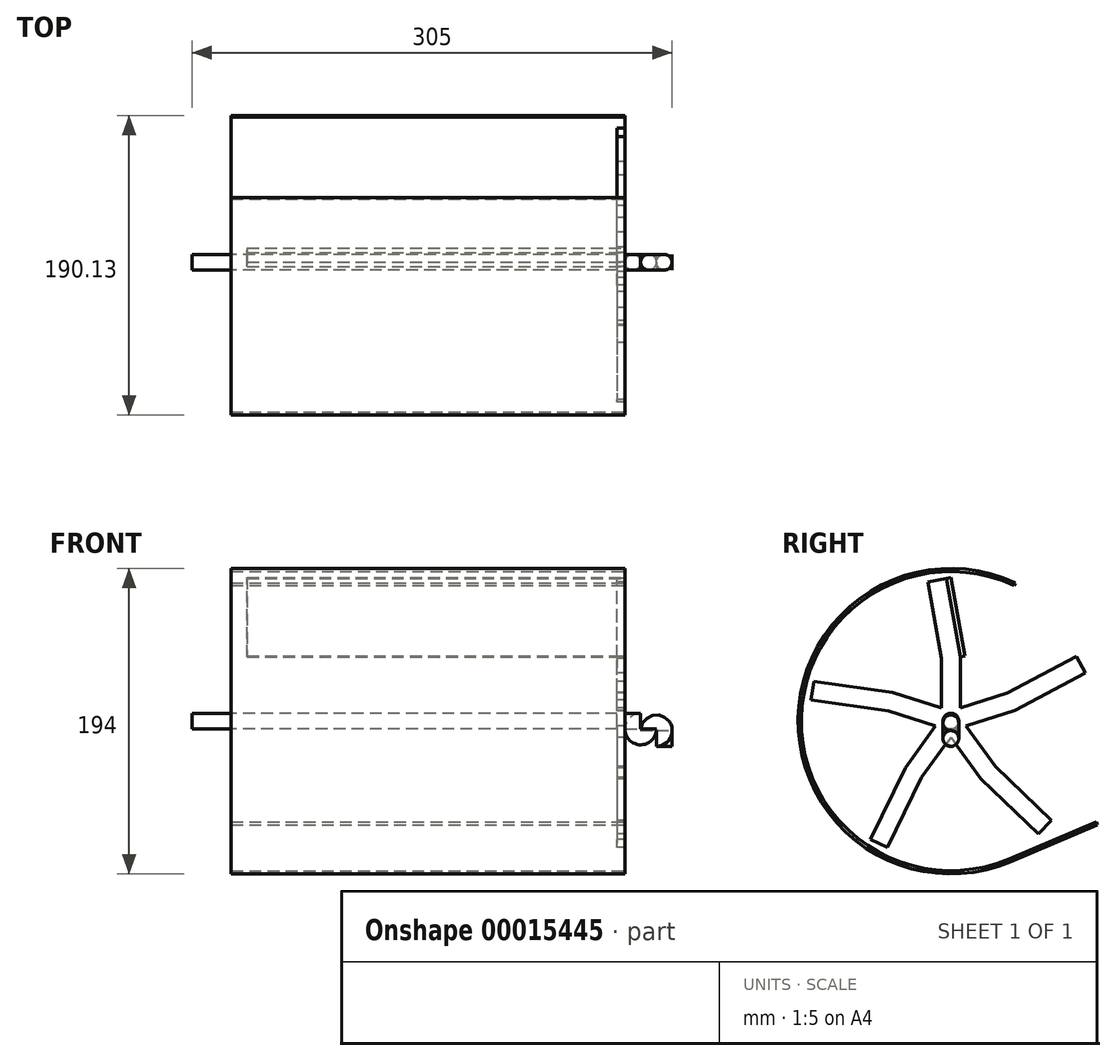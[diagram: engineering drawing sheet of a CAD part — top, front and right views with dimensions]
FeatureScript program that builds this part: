
annotation { "Feature Type Name" : "Feature", "Feature Type Description" : "" }
export const myFeature = defineFeature(function(context is Context, id is Id, definition is map)
    precondition{}
    {
        {
            var Q0;
            Q0=qCreatedBy(makeId("Right.planeOp"),FACE);
            var sketch = newSketch(context, id + "F0", { "sketchPlane" : qUnion([Q0])});
            skCircle(sketch, "E0", {"center": v(0, 0) * mm, "radius": 5 * mm});
            skSolve(sketch);
        }
        {
            var Q0;
            Q0 = qSketchRegion(id + "F0", true);
            extrude(context, id + "F1", {"entities" : qUnion([Q0]), "depth" : 270 * mm});
        }
        {
            var Q0;
            Q0=makeQuery(id+"F1.opExtrude","CAP_FACE",FACE,{"disambiguationData":[OSD([sQuery(id+"F0.wireOp",EDGE,"E0")])],"isStart":false});
            var sketch = newSketch(context, id + "F2", { "sketchPlane" : qUnion([Q0])});
            skLineSegment(sketch, "E1", {"start": v(0, 0) * mm, "end": v(0, 40.34) * mm, "construction": true});
            skLineSegment(sketch, "E2", {"start": v(0, 40.34) * mm, "end": v(-8.68, 89.58) * mm, "construction": true});
            skLineSegment(sketch, "E3.0", {"start": v(6, 40.86) * mm, "end": v(-2.77, 90.62) * mm});
            skLineSegment(sketch, "E3.1", {"start": v(6, 0) * mm, "end": v(6, 40.86) * mm});
            skLineSegment(sketch, "E4.0", {"start": v(-6, 39.81) * mm, "end": v(-14.6, 88.54) * mm});
            skLineSegment(sketch, "E4.1", {"start": v(-6, 0) * mm, "end": v(-6, 39.81) * mm});
            skLineSegment(sketch, "E5", {"start": v(-14.6, 88.54) * mm, "end": v(-2.77, 90.62) * mm});
            skLineSegment(sketch, "E6.1.0", {"start": v(1.85, 5.7) * mm, "end": v(-37.01, 18.33) * mm});
            skLineSegment(sketch, "E6.1.1", {"start": v(-37.01, 18.33) * mm, "end": v(-87.04, 25.37) * mm});
            skLineSegment(sketch, "E6.1.2", {"start": v(-88.71, 13.48) * mm, "end": v(-87.04, 25.37) * mm});
            skLineSegment(sketch, "E6.1.3", {"start": v(-39.72, 6.6) * mm, "end": v(-88.71, 13.48) * mm});
            skLineSegment(sketch, "E6.1.4", {"start": v(-1.85, -5.7) * mm, "end": v(-39.72, 6.6) * mm});
            skLineSegment(sketch, "E6.2.0", {"start": v(-4.85, 3.53) * mm, "end": v(-28.87, -29.53) * mm});
            skLineSegment(sketch, "E6.2.1", {"start": v(-28.87, -29.53) * mm, "end": v(-51.02, -74.95) * mm});
            skLineSegment(sketch, "E6.2.2", {"start": v(-40.24, -80.2) * mm, "end": v(-51.02, -74.95) * mm});
            skLineSegment(sketch, "E6.2.3", {"start": v(-18.55, -35.74) * mm, "end": v(-40.24, -80.2) * mm});
            skLineSegment(sketch, "E6.2.4", {"start": v(4.85, -3.53) * mm, "end": v(-18.55, -35.74) * mm});
            skLineSegment(sketch, "E6.3.0", {"start": v(-4.85, -3.53) * mm, "end": v(19.17, -36.59) * mm});
            skLineSegment(sketch, "E6.3.1", {"start": v(19.17, -36.59) * mm, "end": v(55.51, -71.68) * mm});
            skLineSegment(sketch, "E6.3.2", {"start": v(63.85, -63.05) * mm, "end": v(55.51, -71.68) * mm});
            skLineSegment(sketch, "E6.3.3", {"start": v(28.26, -28.68) * mm, "end": v(63.85, -63.05) * mm});
            skLineSegment(sketch, "E6.3.4", {"start": v(4.85, 3.53) * mm, "end": v(28.26, -28.68) * mm});
            skLineSegment(sketch, "E6.4.0", {"start": v(1.85, -5.7) * mm, "end": v(40.72, 6.92) * mm});
            skLineSegment(sketch, "E6.4.1", {"start": v(40.72, 6.92) * mm, "end": v(85.33, 30.64) * mm});
            skLineSegment(sketch, "E6.4.2", {"start": v(79.7, 41.24) * mm, "end": v(85.33, 30.64) * mm});
            skLineSegment(sketch, "E6.4.3", {"start": v(36.01, 18) * mm, "end": v(79.7, 41.24) * mm});
            skLineSegment(sketch, "E6.4.4", {"start": v(-1.85, 5.7) * mm, "end": v(36.01, 18) * mm});
            skPoint(sketch, "E6.center", {"position": v(0, 0) * mm});
            skSolve(sketch);
        }
        {
            var Q0;
            {var subQ8=sQuery(id+"F2.wireOp",EDGE,"E3.0");Q0=makeQuery(id+"F2.imprint","IMPRINT",FACE,{"disambiguationData":[TD([[makeQuery(id+"F2.imprint","IMPRINT",EDGE,{"derivedFrom":subQ8}),1.0]])]});}
            var Q1;
            {var subQ4=sQuery(id+"F2.wireOp",EDGE,"E6.4.1");Q1=makeQuery(id+"F2.imprint","IMPRINT",FACE,{"disambiguationData":[TD([[makeQuery(id+"F2.imprint","IMPRINT",EDGE,{"derivedFrom":subQ4}),1.0]])]});}
            var Q2;
            {var subQ6=sQuery(id+"F2.wireOp",EDGE,"E6.1.1");Q2=makeQuery(id+"F2.imprint","IMPRINT",FACE,{"disambiguationData":[TD([[makeQuery(id+"F2.imprint","IMPRINT",EDGE,{"derivedFrom":subQ6}),1.0]])]});}
            var Q3;
            {var subQ6=sQuery(id+"F2.wireOp",EDGE,"E6.2.1");Q3=makeQuery(id+"F2.imprint","IMPRINT",FACE,{"disambiguationData":[TD([[makeQuery(id+"F2.imprint","IMPRINT",EDGE,{"derivedFrom":subQ6}),1.0]])]});}
            var Q4;
            {var subQ6=sQuery(id+"F2.wireOp",EDGE,"E6.3.1");Q4=makeQuery(id+"F2.imprint","IMPRINT",FACE,{"disambiguationData":[TD([[makeQuery(id+"F2.imprint","IMPRINT",EDGE,{"derivedFrom":subQ6}),1.0]])]});}
            var Q5;
            Q5=makeQuery(id+"F2.imprint","IMPRINT",FACE,{"disambiguationData":[TD([[makeQuery(id+"F2.imprint","IMPRINT",EDGE,{"derivedFrom":makeQuery(id+"F1.opExtrude","CAP_EDGE",EDGE,{"disambiguationData":[OSD([sQuery(id+"F0.wireOp",EDGE,"E0")])],"isStart":false})}),-1.0]])]});
            extrude(context, id + "F3", {"entities" : qUnion([Q0, Q1, Q2, Q3, Q4, Q5]), "depth" : 5 * mm});
        }
        {
            var Q0;
            Q0=makeQuery(id+"F3.opExtrude","CAP_FACE",FACE,{"disambiguationData":[OSD([sQuery(id+"F0.wireOp",EDGE,"E0"),sQuery(id+"F2.wireOp",EDGE,"E3.0"),sQuery(id+"F2.wireOp",EDGE,"E3.1"),sQuery(id+"F2.wireOp",EDGE,"E4.0"),sQuery(id+"F2.wireOp",EDGE,"E4.1"),sQuery(id+"F2.wireOp",EDGE,"E5"),sQuery(id+"F2.wireOp",EDGE,"E6.1.0"),sQuery(id+"F2.wireOp",EDGE,"E6.1.1"),sQuery(id+"F2.wireOp",EDGE,"E6.1.2"),sQuery(id+"F2.wireOp",EDGE,"E6.1.3"),sQuery(id+"F2.wireOp",EDGE,"E6.1.4"),sQuery(id+"F2.wireOp",EDGE,"E6.2.0"),sQuery(id+"F2.wireOp",EDGE,"E6.2.1"),sQuery(id+"F2.wireOp",EDGE,"E6.2.2"),sQuery(id+"F2.wireOp",EDGE,"E6.2.3"),sQuery(id+"F2.wireOp",EDGE,"E6.2.4"),sQuery(id+"F2.wireOp",EDGE,"E6.3.0"),sQuery(id+"F2.wireOp",EDGE,"E6.3.1"),sQuery(id+"F2.wireOp",EDGE,"E6.3.2"),sQuery(id+"F2.wireOp",EDGE,"E6.3.3"),sQuery(id+"F2.wireOp",EDGE,"E6.3.4"),sQuery(id+"F2.wireOp",EDGE,"E6.4.0"),sQuery(id+"F2.wireOp",EDGE,"E6.4.1"),sQuery(id+"F2.wireOp",EDGE,"E6.4.2"),sQuery(id+"F2.wireOp",EDGE,"E6.4.3"),sQuery(id+"F2.wireOp",EDGE,"E6.4.4")])],"isStart":false});
            var sketch = newSketch(context, id + "F4", { "sketchPlane" : qUnion([Q0])});
            skLineSegment(sketch, "E7.0", {"start": v(6, 40.86) * mm, "end": v(-2.77, 90.62) * mm});
            skLineSegment(sketch, "E8", {"start": v(-2.77, 90.62) * mm, "end": v(0.18, 91.14) * mm});
            skLineSegment(sketch, "E9", {"start": v(0.18, 91.14) * mm, "end": v(8.95, 41.39) * mm});
            skLineSegment(sketch, "E10", {"start": v(8.95, 41.39) * mm, "end": v(6, 40.86) * mm});
            skSolve(sketch);
        }
        {
            var Q0;
            Q0 = qSketchRegion(id + "F4", true);
            extrude(context, id + "F5", {"entities" : qUnion([Q0]), "oppositeDirection" : true, "depth" : 240 * mm});
        }
        {
            var Q0;
            Q0=makeQuery(id+"F3.opExtrude","CAP_FACE",FACE,{"disambiguationData":[OSD([sQuery(id+"F0.wireOp",EDGE,"E0"),sQuery(id+"F2.wireOp",EDGE,"E3.0"),sQuery(id+"F2.wireOp",EDGE,"E3.1"),sQuery(id+"F2.wireOp",EDGE,"E4.0"),sQuery(id+"F2.wireOp",EDGE,"E4.1"),sQuery(id+"F2.wireOp",EDGE,"E5"),sQuery(id+"F2.wireOp",EDGE,"E6.1.0"),sQuery(id+"F2.wireOp",EDGE,"E6.1.1"),sQuery(id+"F2.wireOp",EDGE,"E6.1.2"),sQuery(id+"F2.wireOp",EDGE,"E6.1.3"),sQuery(id+"F2.wireOp",EDGE,"E6.1.4"),sQuery(id+"F2.wireOp",EDGE,"E6.2.0"),sQuery(id+"F2.wireOp",EDGE,"E6.2.1"),sQuery(id+"F2.wireOp",EDGE,"E6.2.2"),sQuery(id+"F2.wireOp",EDGE,"E6.2.3"),sQuery(id+"F2.wireOp",EDGE,"E6.2.4"),sQuery(id+"F2.wireOp",EDGE,"E6.3.0"),sQuery(id+"F2.wireOp",EDGE,"E6.3.1"),sQuery(id+"F2.wireOp",EDGE,"E6.3.2"),sQuery(id+"F2.wireOp",EDGE,"E6.3.3"),sQuery(id+"F2.wireOp",EDGE,"E6.3.4"),sQuery(id+"F2.wireOp",EDGE,"E6.4.0"),sQuery(id+"F2.wireOp",EDGE,"E6.4.1"),sQuery(id+"F2.wireOp",EDGE,"E6.4.2"),sQuery(id+"F2.wireOp",EDGE,"E6.4.3"),sQuery(id+"F2.wireOp",EDGE,"E6.4.4")])],"isStart":false});
            var sketch = newSketch(context, id + "F6", { "sketchPlane" : qUnion([Q0])});
            skLineSegment(sketch, "E11", {"start": v(0, 0) * mm, "end": v(41, 87.91) * mm, "construction": true});
            skLineSegment(sketch, "E12", {"start": v(0, 0) * mm, "end": v(37.9, -89.29) * mm, "construction": true});
            skLineSegment(sketch, "E13", {"start": v(0, 0) * mm, "end": v(0, -97) * mm, "construction": true});
            skArc(sketch, "E14", {"start": v(41, 87.91) * mm, "mid": v(-96.99, 1.7) * mm, "end": v(37.9, -89.29) * mm});
            skArc(sketch, "E15", {"start": v(37.9, -89.29) * mm, "mid": v(96.99, -1.7) * mm, "end": v(41, 87.91) * mm, "construction": true});
            skArc(sketch, "E16", {"start": v(37.12, -87.45) * mm, "mid": v(94.99, -1.66) * mm, "end": v(40.15, 86.1) * mm, "construction": true});
            skArc(sketch, "E17", {"start": v(40.15, 86.1) * mm, "mid": v(-94.99, 1.66) * mm, "end": v(37.12, -87.45) * mm});
            skLineSegment(sketch, "E18", {"start": v(41, 87.91) * mm, "end": v(40.15, 86.1) * mm});
            skLineSegment(sketch, "E19", {"start": v(37.12, -87.45) * mm, "end": v(37.9, -89.29) * mm});
            skSolve(sketch);
        }
        {
            var Q0;
            Q0 = qSketchRegion(id + "F6", true);
            extrude(context, id + "F7", {"entities" : qUnion([Q0]), "oppositeDirection" : true, "depth" : 250 * mm});
        }
        {
            var Q0;
            Q0=makeQuery(id+"F7.opExtrude","SWEPT_FACE",FACE,{"disambiguationData":[OSD([sQuery(id+"F6.wireOp",EDGE,"E19")])]});
            extrude(context, id + "F8", {"entities" : qUnion([Q0]), "operationType" : NewBodyOperationType.ADD, "depth" : 60 * mm});
        }
        {
            var Q0;
            Q0=qCreatedBy(makeId("Front.planeOp"),FACE);
            var sketch = newSketch(context, id + "F9", { "sketchPlane" : qUnion([Q0])});
            skFitSpline(sketch, "E20", {"points": [v(0, 0) * mm, v(-25, -12.5) * mm, v(-25, -37.5) * mm, v(-50, -50) * mm], "startDerivative": vector(-220.93, 0) * mm, "endDerivative": vector(-220.93, 0) * mm});
            skSolve(sketch);
        }
        {
            var Q0;
            Q0=qCreatedBy(makeId("Front.planeOp"),FACE);
            var sketch = newSketch(context, id + "F10", { "sketchPlane" : qUnion([Q0])});
            skLineSegment(sketch, "E21.0", {"start": v(270, 5) * mm, "end": v(270, -5) * mm, "construction": true});
            skLineSegment(sketch, "E22", {"start": v(270, 0) * mm, "end": v(285, 0) * mm});
            skLineSegment(sketch, "E23", {"start": v(290, -5) * mm, "end": v(290, -6) * mm});
            skLineSegment(sketch, "E24", {"start": v(295, -11) * mm, "end": v(305, -11) * mm});
            skArc(sketch, "E25", {"start": v(290, -5) * mm, "mid": v(288.54, -1.46) * mm, "end": v(285, 0) * mm});
            skArc(sketch, "E26", {"start": v(290, -6) * mm, "mid": v(291.46, -9.54) * mm, "end": v(295, -11) * mm});
            skSolve(sketch);
        }
        {
            var Q0;
            Q0=makeQuery(id+"F1.opExtrude","CAP_FACE",FACE,{"disambiguationData":[OSD([sQuery(id+"F0.wireOp",EDGE,"E0")])],"isStart":false});
            var Q1;
            Q1 = qConstructionFilter(qBodyType(qCreatedBy(id + "F10" ,EDGE), BodyType.WIRE), ConstructionObject.NO);
            sweep(context, id + "F11", {"operationType" : NewBodyOperationType.ADD, "profiles" : qUnion([Q0]), "path" : qUnion([Q1])});
        }
    });
